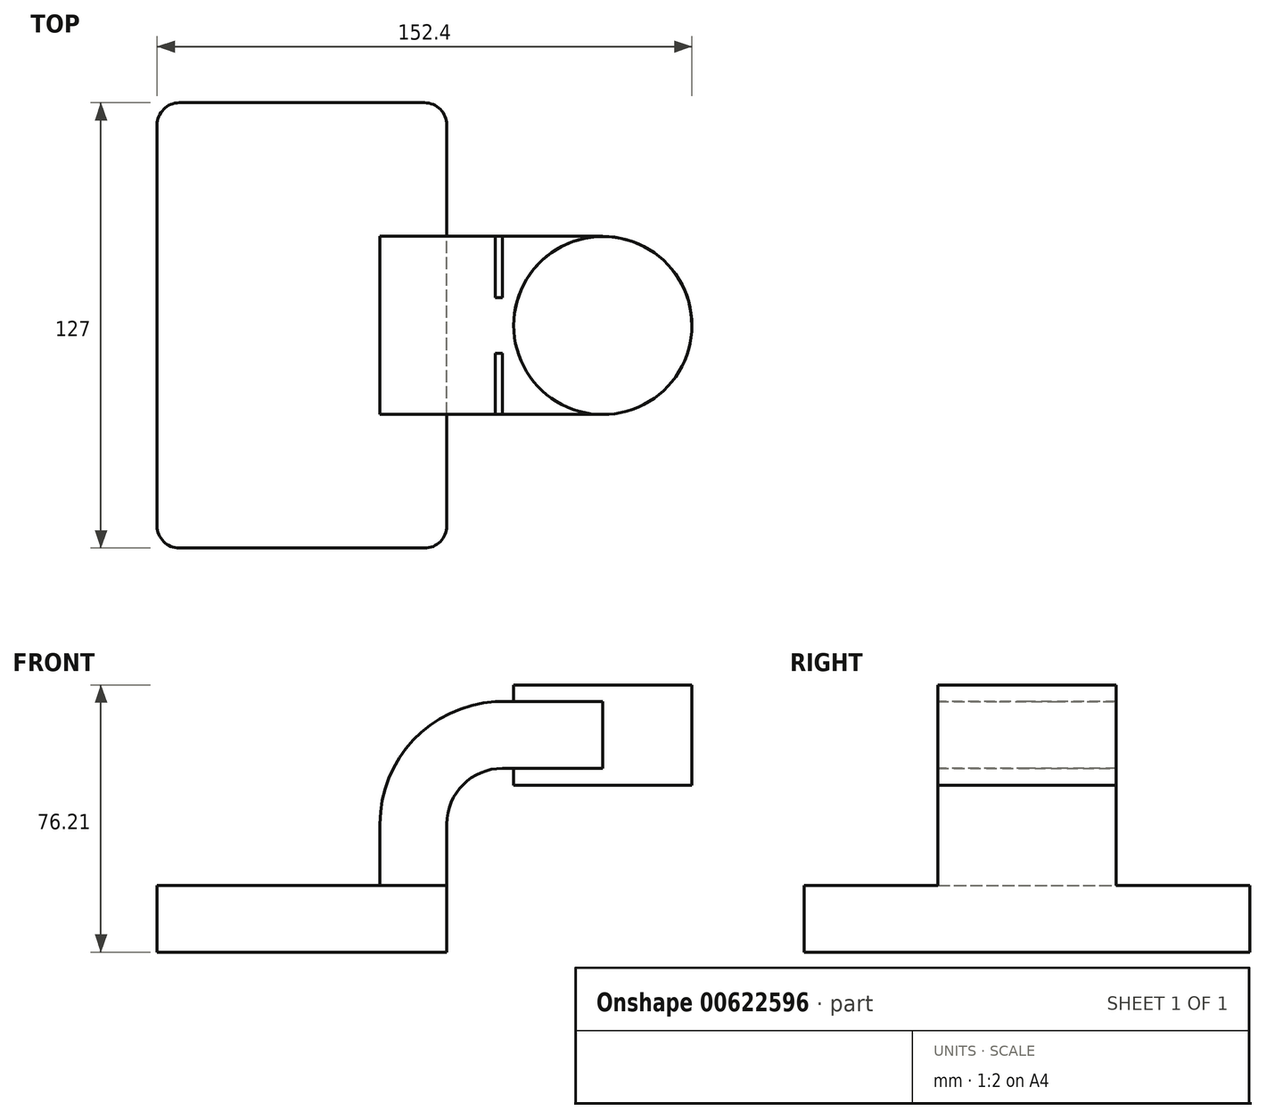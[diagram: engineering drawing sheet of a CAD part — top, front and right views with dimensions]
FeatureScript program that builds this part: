
annotation { "Feature Type Name" : "Feature", "Feature Type Description" : "" }
export const myFeature = defineFeature(function(context is Context, id is Id, definition is map)
    precondition{}
    {
        {
            var Q0;
            Q0=qCreatedBy(makeId("Front.planeOp"),FACE);
            var sketch = newSketch(context, id + "F0", { "sketchPlane" : qUnion([Q0])});
            skLineSegment(sketch, "E0.bottom", {"start": v(41.28, -9.52) * mm, "end": v(-41.28, -9.53) * mm});
            skLineSegment(sketch, "E0.top", {"start": v(41.28, 9.53) * mm, "end": v(-41.28, 9.53) * mm});
            skLineSegment(sketch, "E0.left", {"start": v(41.28, -9.52) * mm, "end": v(41.28, 9.53) * mm});
            skLineSegment(sketch, "E0.right", {"start": v(-41.28, -9.52) * mm, "end": v(-41.28, 9.53) * mm});
            skPoint(sketch, "E0.middle", {"position": v(0, 0) * mm});
            skLineSegment(sketch, "E1.bottom", {"start": v(111.12, 38.1) * mm, "end": v(60.32, 38.1) * mm});
            skLineSegment(sketch, "E1.top", {"start": v(111.12, 66.68) * mm, "end": v(60.32, 66.68) * mm});
            skLineSegment(sketch, "E1.left", {"start": v(111.12, 38.1) * mm, "end": v(111.12, 66.68) * mm});
            skLineSegment(sketch, "E1.right", {"start": v(60.32, 38.1) * mm, "end": v(60.32, 66.68) * mm});
            skPoint(sketch, "E1.middle", {"position": v(85.72, 52.39) * mm});
            skLineSegment(sketch, "E2", {"start": v(41.28, 9.53) * mm, "end": v(41.28, 27) * mm});
            skArc(sketch, "E3", {"start": v(41.27, 27) * mm, "mid": v(45.92, 38.23) * mm, "end": v(57.15, 42.88) * mm});
            skLineSegment(sketch, "E4", {"start": v(57.15, 42.88) * mm, "end": v(85.73, 42.88) * mm});
            skLineSegment(sketch, "E5.0", {"start": v(57.15, 61.93) * mm, "end": v(85.73, 61.93) * mm});
            skArc(sketch, "E5.1", {"start": v(22.23, 27) * mm, "mid": v(32.45, 51.7) * mm, "end": v(57.15, 61.93) * mm});
            skLineSegment(sketch, "E5.2", {"start": v(22.22, 9.53) * mm, "end": v(22.22, 27) * mm});
            skLineSegment(sketch, "E6", {"start": v(85.72, 38.1) * mm, "end": v(85.73, 66.68) * mm});
            skFitSpline(sketch, "E7", {"points": [v(-41.28, 9.53) * mm, v(57.15, 61.93) * mm], "startDerivative": vector(105.46, 131.82) * mm, "endDerivative": vector(171.45, 4.9) * mm});
            skSolve(sketch);
        }
        {
            var Q0;
            Q0=makeQuery(id+"F0.imprint","IMPRINT",FACE,{"disambiguationData":[TD([[makeQuery(id+"F0.imprint","IMPRINT",EDGE,{"derivedFrom":sQuery(id+"F0.wireOp",EDGE,"E0.bottom")}),-1.0]])]});
            extrude(context, id + "F1", {"entities" : qUnion([Q0]), "endBound" : BoundingType.SYMMETRIC, "depth" : 127 * mm, "offsetDistance" : 25.4 * mm});
        }
        {
            var Q0;
            {var subQ0=sQuery(id+"F0.wireOp",EDGE,"E4");var subQ1=sQuery(id+"F0.wireOp",EDGE,"E1.right");var subQ2=makeQuery(id+"F0.imprint","INTERSECT",VERTEX,{"derivedFrom":[subQ1,subQ0]});Q0=makeQuery(id+"F0.imprint","IMPRINT",FACE,{"disambiguationData":[TD([[makeQuery(id+"F0.imprint","IMPRINT",EDGE,{"disambiguationData":[TD([[subQ2,-1.0]])],"derivedFrom":subQ1}),-1.0]])]});}
            var Q1;
            {var subQ5=sQuery(id+"F0.wireOp",EDGE,"E2");Q1=makeQuery(id+"F0.imprint","IMPRINT",FACE,{"disambiguationData":[TD([[makeQuery(id+"F0.imprint","IMPRINT",EDGE,{"derivedFrom":subQ5}),1.0]])]});}
            extrude(context, id + "F2", {"entities" : qUnion([Q0, Q1]), "operationType" : NewBodyOperationType.ADD, "endBound" : BoundingType.SYMMETRIC, "depth" : 50.8 * mm, "offsetDistance" : 25.4 * mm});
        }
        {
            var Q0;
            {var subQ4=sQuery(id+"F0.wireOp",EDGE,"E5.1");Q0=makeQuery(id+"F0.imprint","IMPRINT",FACE,{"disambiguationData":[TD([[makeQuery(id+"F0.imprint","IMPRINT",EDGE,{"derivedFrom":subQ4}),1.0]])]});}
            extrude(context, id + "F3", {"entities" : qUnion([Q0]), "operationType" : NewBodyOperationType.ADD, "endBound" : BoundingType.SYMMETRIC, "depth" : 15.88 * mm, "offsetDistance" : 25.4 * mm});
        }
        {
            var Q0;
            {var subQ4=sQuery(id+"F0.wireOp",EDGE,"E1.left");Q0=makeQuery(id+"F0.imprint","IMPRINT",FACE,{"disambiguationData":[TD([[makeQuery(id+"F0.imprint","IMPRINT",EDGE,{"derivedFrom":subQ4}),1.0]])]});}
            var Q1;
            Q1=sQuery(id+"F0.wireOp",EDGE,"E6");
            revolve(context, id + "F4", {"operationType" : NewBodyOperationType.ADD, "entities" : qUnion([Q0]), "axis" : qUnion([Q1]), "revolveType" : RevolveType.FULL});
        }
        {
            var Q0;
            Q0=makeQuery(id+"F1.opExtrude","CAP_EDGE",EDGE,{"disambiguationData":[OSD([sQuery(id+"F0.wireOp",EDGE,"E0.right")])],"isStart":false});
            var Q1;
            Q1=makeQuery(id+"F1.opExtrude","CAP_EDGE",EDGE,{"disambiguationData":[OSD([sQuery(id+"F0.wireOp",EDGE,"E0.left")])],"isStart":false});
            var Q2;
            Q2=makeQuery(id+"F1.opExtrude","CAP_EDGE",EDGE,{"disambiguationData":[OSD([sQuery(id+"F0.wireOp",EDGE,"E0.left")])],"isStart":true});
            var Q3;
            Q3=makeQuery(id+"F1.opExtrude","CAP_EDGE",EDGE,{"disambiguationData":[OSD([sQuery(id+"F0.wireOp",EDGE,"E0.right")])],"isStart":true});
            fillet(context, id + "F5", {"entities" : qUnion([Q0, Q1, Q2, Q3]), "radius" : 6.35 * mm, "tangentPropagation" : true, "allowEdgeOverflow" : false});
        }
    });
